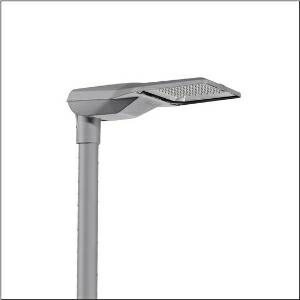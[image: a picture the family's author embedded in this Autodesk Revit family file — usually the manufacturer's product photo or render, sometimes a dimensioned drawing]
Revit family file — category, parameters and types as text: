
# Revit family: streetlight_sl_21_iq_midi___stw1_0a_5xe3e31g08mb_59a2
name_source: partatom
category: Lighting Fixtures
units: mm (PartAtom-declared; Revit-internal decimal feet)

## family parameters
Cut with Voids When Loaded = No
Host = Face
Light Source = No
Part Type = Normal
Room Calculation Point = No
Round Connector Dimension = Use Diameter
Shared = No

## types (1)
- --- (1 x LED, 19500 lm, 146.7 W, 3000K)
    Apparent Load = 147 VA
    CIE Flux Codes = 38 75 98 100 100
    Color Rendering = 70
    Color Temperature = 3000K
    Default Elevation = 1800 mm
    Description = Streetlight SL 21 iQ midi, mast luminaire, primary light control with lens, of PMMA, primary optical cover: cover, of toughened safety glass, transparent, light distribution: STW1.0a, light emission: direct distribution, primary light characteristic: asymmetric, installation type: post-top, side-entry, LED, High Power LED, rated luminous flux: 19.500lm, luminous efficacy: 133lm/W, light colour: 730, colour temperature: 3000K, control gear: iQ Street-Remote, control: Street-Remote, Auto-Match, Temp-Guard, Lumen-Switch, Night-Set, Smart-Wire, Light-Fading, Desk-Remote (wireless, voltage-free reading and setting of iQ features in the workshop via application-optimized NFC function/RFID function), optimised constant luminous flux control (CLO 2.0), pre-setting: linear dimming characteristic, mains connection: 230..240V, AC, 50/60Hz, start of lifetime: 147W, end of service life: 161W, reduction: 62W, luminaire housing, of diecast aluminium, powder-coated, Siteco® metallic grey (DB 702S), corrosivity category C5 mid according to DIN EN ISO 12944, please order mast flange separately, inclination adjustable: 0°, 5°, 10°, 15°, sealing non-destructively replaceable, multi-level sealing system, length: 644mm, width: 335mm, height: 110mm, mast flange for spigot size: 42mm (side-entry): 5XC10008XM4, 60/48mm (side-entry/post-top): 5XC10108XM2, 76/60mm (side-entry/post-top): 5XC10108XM1, mounting height: 4..8m, protection rating (complete): IP66, insulation class (complete): insulation class II (safety insulation), certification: CE, ENEC, ENEC+, VDE, impact resistance: IK10, permissible operating ambient temperature for outdoor applications: -40..+50°C, standard-compliant lighting for roads and squares, packaging unit: 1 piece

Light Distribution: STW1.0a
    Height = 111 mm
    Lamp = 1 x LED
    Lamp Light Flux = 19500 lm
    Lamp Power = 146.7 W
    Lamp count = 1
    Length = 644 mm
    Luminous efficacy = 133 lm/W
    Manufacturer = Siteco
    ModVariant = No
    Model = 5XE3E31G08MB
    Number of Poles = 1
    OnlyDefault = Yes
    Power Factor = 1
    Product Name = Streetlight SL 21 iQ midi | STW1.0a
    Product group = mast luminaire | pylon top
    ProductGroupID = 6100
    Protection Class = Protection class II
    Protection Degree = IP 66
    RLX_Detail_Level = 1
    RLX_Emergency_Light_Flux = 0 lm
    RLX_Emergency_Type = 0
    RLX_Emergency_Type_DB = No
    RlxData = <blob elided: 26993 chars, md5=954fc483>
    Socket = socket
    Standby Power = 0 W
    System Light Flux = 19499 lm
    System Power = 147 W
    Type Comments = factory setting: luminous flux: 100 % | dim-lin: 254 | 753 mA
    Type Image = l_1004298.jpg
    URL = http://relux.com
    VarID = @adj_209399
    Voltage = 0 V
    Weight = 0.00 kg
    Width = 336 mm

## geometry (parser evidence)
native form markers: Blend x4, Sweep x11
no freeform markers — native parametric forms only
